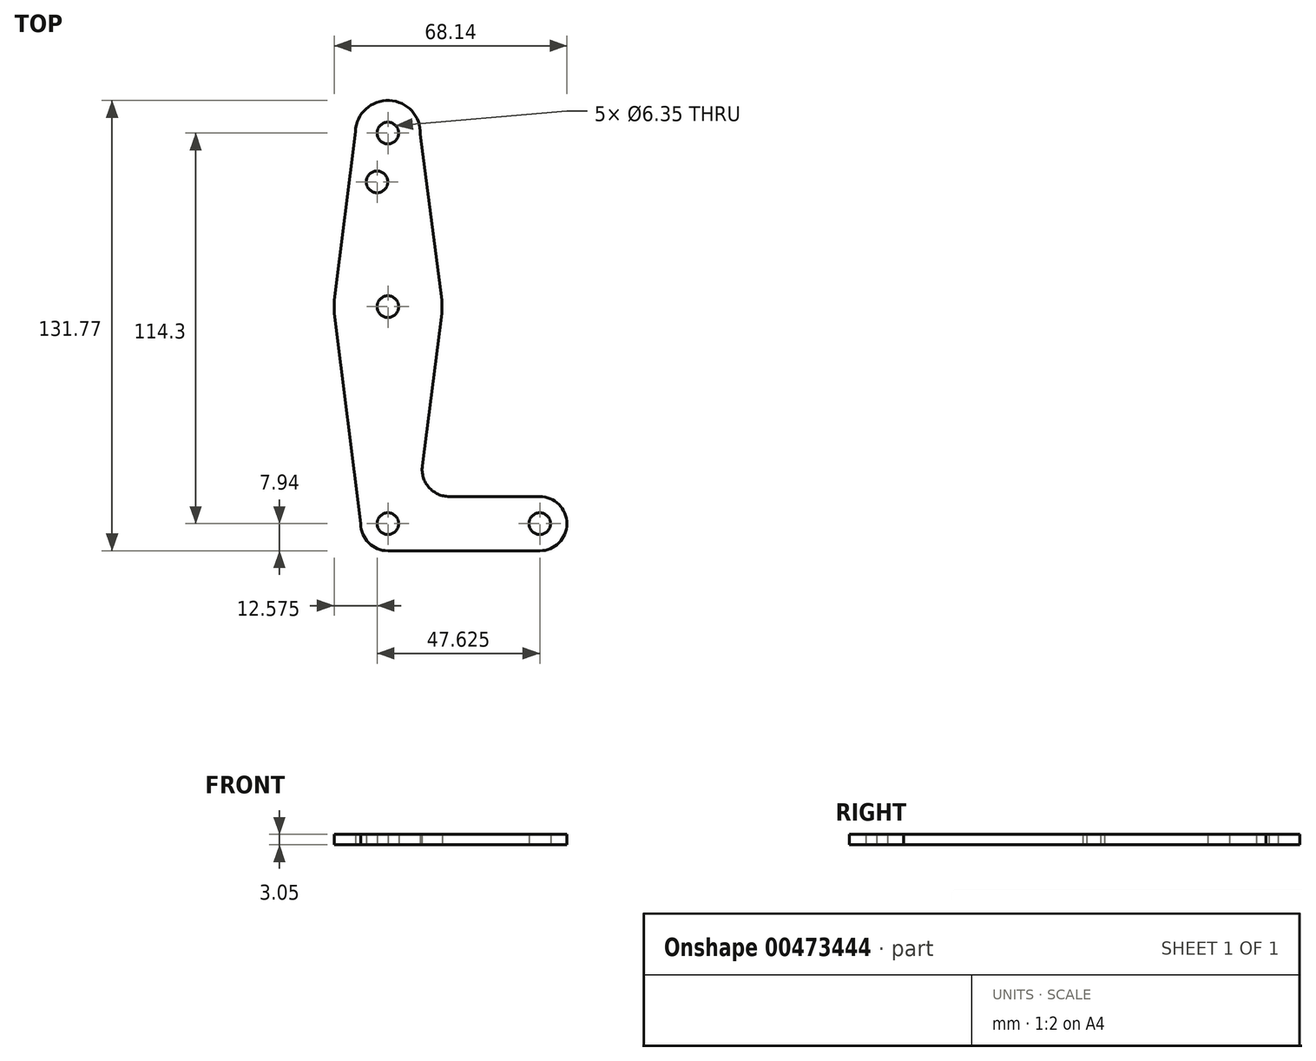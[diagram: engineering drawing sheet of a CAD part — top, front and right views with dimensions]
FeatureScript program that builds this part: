
annotation { "Feature Type Name" : "Feature", "Feature Type Description" : "" }
export const myFeature = defineFeature(function(context is Context, id is Id, definition is map)
    precondition{}
    {
        {
            var Q0;
            Q0=qCreatedBy(makeId("Top.planeOp"),FACE);
            var sketch = newSketch(context, id + "F0", { "sketchPlane" : qUnion([Q0])});
            skLineSegment(sketch, "E0", {"start": v(0, 0) * mm, "end": v(0, 114.3) * mm, "construction": true});
            skLineSegment(sketch, "E1", {"start": v(0, 0) * mm, "end": v(44.45, 0) * mm, "construction": true});
            skCircle(sketch, "E2", {"center": v(0, 0) * mm, "radius": 7.94 * mm});
            skCircle(sketch, "E3", {"center": v(0, 114.3) * mm, "radius": 9.53 * mm});
            skCircle(sketch, "E4", {"center": v(44.45, 0) * mm, "radius": 7.94 * mm});
            skCircle(sketch, "E5", {"center": v(0, 63.5) * mm, "radius": 15.88 * mm});
            skLineSegment(sketch, "E6", {"start": v(-9.51, 114.78) * mm, "end": v(-15.75, 65.5) * mm});
            skLineSegment(sketch, "E7", {"start": v(-15.75, 65.5) * mm, "end": v(-15.75, 61.5) * mm});
            skLineSegment(sketch, "E8", {"start": v(0, -7.94) * mm, "end": v(44.45, -7.94) * mm});
            skLineSegment(sketch, "E9", {"start": v(44.45, -7.94) * mm, "end": v(44.45, 7.94) * mm});
            skLineSegment(sketch, "E10", {"start": v(44.45, 7.94) * mm, "end": v(17.97, 7.94) * mm});
            skLineSegment(sketch, "E11", {"start": v(10.08, 16.89) * mm, "end": v(15.75, 61.5) * mm});
            skLineSegment(sketch, "E12", {"start": v(9.52, 113.95) * mm, "end": v(15.75, 65.5) * mm});
            skCircle(sketch, "E13", {"center": v(0, 114.3) * mm, "radius": 3.18 * mm});
            skCircle(sketch, "E14", {"center": v(0, 63.5) * mm, "radius": 3.18 * mm});
            skCircle(sketch, "E15", {"center": v(0, 0) * mm, "radius": 3.18 * mm});
            skCircle(sketch, "E16", {"center": v(44.45, 0) * mm, "radius": 3.18 * mm});
            skCircle(sketch, "E17", {"center": v(-3.18, 100.03) * mm, "radius": 3.18 * mm});
            skArc(sketch, "E18.filletArc", {"start": v(10.08, 16.89) * mm, "mid": v(12, 10.63) * mm, "end": v(17.97, 7.94) * mm});
            skLineSegment(sketch, "E19", {"start": v(-7.94, 0) * mm, "end": v(-15.75, 61.5) * mm});
            skSolve(sketch);
        }
        {
            var Q0;
            {var subQ0=sQuery(id+"F0.wireOp",EDGE,"E8");Q0=makeQuery(id+"F0.imprint","IMPRINT",FACE,{"disambiguationData":[TD([[makeQuery(id+"F0.imprint","IMPRINT",EDGE,{"derivedFrom":subQ0}),1.0]])]});}
            var Q1;
            Q1=makeQuery(id+"F0.imprint","IMPRINT",FACE,{"disambiguationData":[TD([[makeQuery(id+"F0.imprint","IMPRINT",EDGE,{"derivedFrom":sQuery(id+"F0.wireOp",EDGE,"E15")}),-1.0]])]});
            var Q2;
            {var subQ0=sQuery(id+"F0.wireOp",EDGE,"E9");var subQ4=sQuery(id+"F0.wireOp",EDGE,"E16");var subQ5=makeQuery(id+"F0.imprint","INTERSECT",VERTEX,{"disambiguationData":[OD(0.0)],"derivedFrom":[subQ0,subQ4]});Q2=makeQuery(id+"F0.imprint","IMPRINT",FACE,{"disambiguationData":[TD([[makeQuery(id+"F0.imprint","IMPRINT",EDGE,{"disambiguationData":[TD([[subQ5,1.0]])],"derivedFrom":subQ4}),-1.0]])]});}
            var Q3;
            {var subQ0=sQuery(id+"F0.wireOp",EDGE,"E9");var subQ4=sQuery(id+"F0.wireOp",EDGE,"E16");var subQ5=makeQuery(id+"F0.imprint","INTERSECT",VERTEX,{"disambiguationData":[OD(0.0)],"derivedFrom":[subQ0,subQ4]});Q3=makeQuery(id+"F0.imprint","IMPRINT",FACE,{"disambiguationData":[TD([[makeQuery(id+"F0.imprint","IMPRINT",EDGE,{"disambiguationData":[TD([[subQ5,-1.0]])],"derivedFrom":subQ4}),-1.0]])]});}
            var Q4;
            {var subQ4=sQuery(id+"F0.wireOp",EDGE,"E7");Q4=makeQuery(id+"F0.imprint","IMPRINT",FACE,{"disambiguationData":[TD([[makeQuery(id+"F0.imprint","IMPRINT",EDGE,{"derivedFrom":subQ4}),1.0]])]});}
            var Q5;
            {var subQ1=sQuery(id+"F0.wireOp",EDGE,"E6");Q5=makeQuery(id+"F0.imprint","IMPRINT",FACE,{"disambiguationData":[TD([[makeQuery(id+"F0.imprint","IMPRINT",EDGE,{"derivedFrom":subQ1}),1.0]])]});}
            var Q6;
            Q6=makeQuery(id+"F0.imprint","IMPRINT",FACE,{"disambiguationData":[TD([[makeQuery(id+"F0.imprint","IMPRINT",EDGE,{"derivedFrom":sQuery(id+"F0.wireOp",EDGE,"E13")}),-1.0]])]});
            extrude(context, id + "F1", {"entities" : qUnion([Q0, Q1, Q2, Q3, Q4, Q5, Q6]), "depth" : 3.05 * mm});
        }
    });
